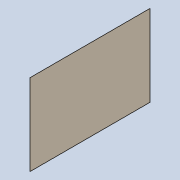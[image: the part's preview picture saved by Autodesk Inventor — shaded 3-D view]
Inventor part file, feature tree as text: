
AUTODESK INVENTOR PART (.ipt)
format: ipt  version: 2022 (Build 260153000, 153)  size: 691,200 bytes
history: native  units: in
note: dims shown in document units (in); Inventor stores cm internally (conversion verified against a paired STEP export)
features: extrude x3, sketch x3, pattern_linear x2
ambient origin geometry x8: Origin, YZ Plane, XZ Plane, XY Plane, X Axis, Y Axis, Z Axis, Center Point
bodies: Solid1 (feature_tree)
feature tree (8):
  extrude  "Extrusion1"  Depth=93.5in
  extrude  "Extrusion2"  Depth=0.25in
  pattern_linear  "Rectangular Pattern1"  Spacing1=7.8505in  [1 undecoded]
  extrude  "Extrusion3"  Depth=0.25in
  pattern_linear  "Rectangular Pattern2"  Spacing1=0.25in  [1 undecoded]
  sketch  "Sketch1"  dims[d0=60.0in d1=93.5in]
  sketch  "Sketch2"  dims[d2=0.25in d3=0.0in d4=0.17in]
  sketch  "Sketch3"  dims[d5=2.1005in d6=7.8505in d7=0.7874in d9=3.299in d10=0.7874in d12=3.299in d15=0.25in d16=0.0in d17=4.7244in d19=4.25in d20=6.2992in d22=4.25in d23=0.17in d24=7.75in d25=2.25in d26=0.25in d27=0.0in d28=0.7874in d30=21.0in d31=0.7874in d33=50.0in]
note: 2 required parameter values undecoded (feature->parameter linkage not recoverable at this tier; creation-order binding heuristic only, values carry confidence <= 0.55)
